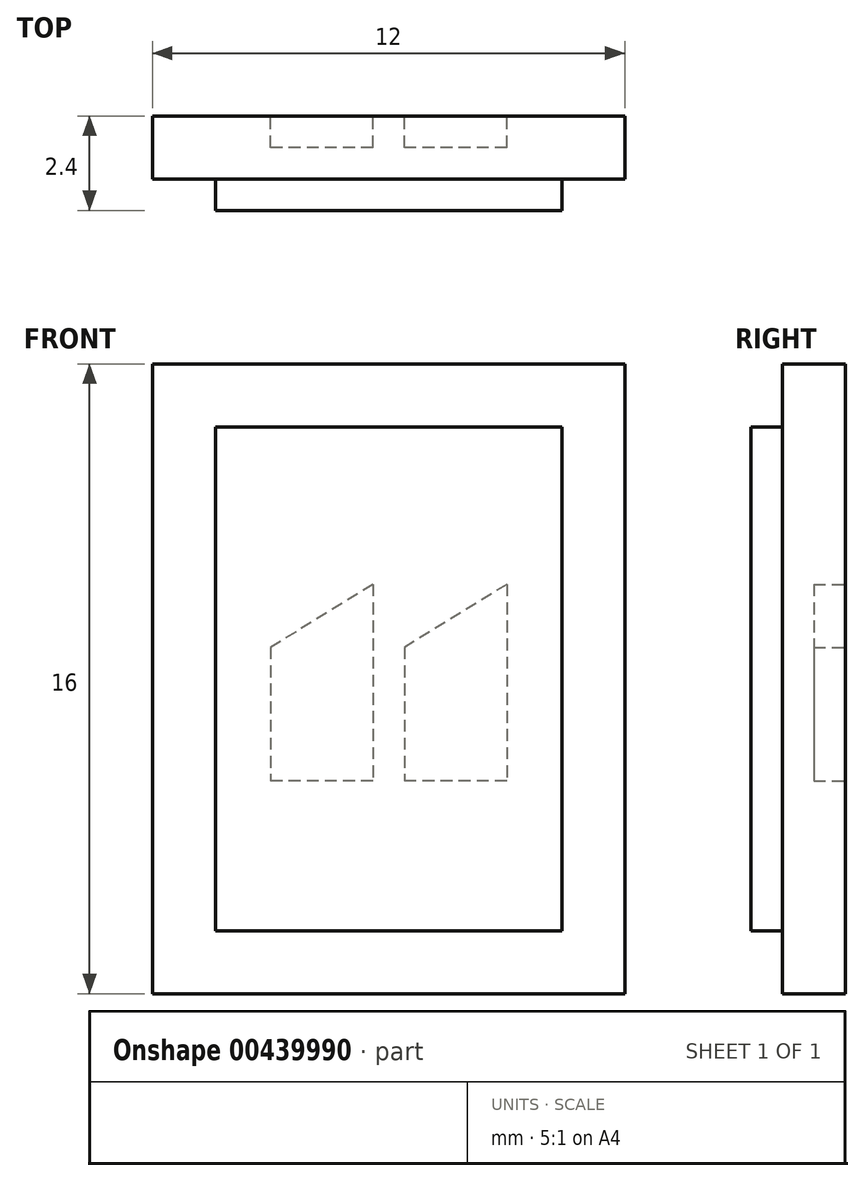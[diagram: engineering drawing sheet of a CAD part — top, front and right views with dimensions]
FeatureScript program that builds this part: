
annotation { "Feature Type Name" : "Feature", "Feature Type Description" : "" }
export const myFeature = defineFeature(function(context is Context, id is Id, definition is map)
    precondition{}
    {
        {
            var Q0;
            Q0=qCreatedBy(makeId("Front.planeOp"),FACE);
            var sketch = newSketch(context, id + "F0", { "sketchPlane" : qUnion([Q0])});
            skLineSegment(sketch, "E0.bottom", {"start": v(0, 0) * mm, "end": v(-12, 0) * mm});
            skLineSegment(sketch, "E0.top", {"start": v(0, 16) * mm, "end": v(-12, 16) * mm});
            skLineSegment(sketch, "E0.left", {"start": v(0, 0) * mm, "end": v(0, 16) * mm});
            skLineSegment(sketch, "E0.right", {"start": v(-12, 0) * mm, "end": v(-12, 16) * mm});
            skLineSegment(sketch, "E1.0", {"start": v(-1.6, 14.4) * mm, "end": v(-10.4, 14.4) * mm});
            skLineSegment(sketch, "E1.1", {"start": v(-1.6, 1.6) * mm, "end": v(-1.6, 14.4) * mm});
            skLineSegment(sketch, "E1.2", {"start": v(-1.6, 1.6) * mm, "end": v(-10.4, 1.6) * mm});
            skLineSegment(sketch, "E1.3", {"start": v(-10.4, 1.6) * mm, "end": v(-10.4, 14.4) * mm});
            skLineSegment(sketch, "E2.bottom", {"start": v(-3, 10.4) * mm, "end": v(-5.6, 10.4) * mm});
            skLineSegment(sketch, "E2.top", {"start": v(-3, 5.4) * mm, "end": v(-5.6, 5.4) * mm});
            skLineSegment(sketch, "E2.left", {"start": v(-3, 10.4) * mm, "end": v(-3, 5.4) * mm});
            skLineSegment(sketch, "E2.right", {"start": v(-5.6, 10.4) * mm, "end": v(-5.6, 5.4) * mm});
            skLineSegment(sketch, "E3.bottom", {"start": v(-6.4, 10.4) * mm, "end": v(-9, 10.4) * mm});
            skLineSegment(sketch, "E3.top", {"start": v(-6.4, 5.4) * mm, "end": v(-9, 5.4) * mm});
            skLineSegment(sketch, "E3.left", {"start": v(-6.4, 10.4) * mm, "end": v(-6.4, 5.4) * mm});
            skLineSegment(sketch, "E3.right", {"start": v(-9, 10.4) * mm, "end": v(-9, 5.4) * mm});
            skPoint(sketch, "E4", {"position": v(-5.6, 8.8) * mm});
            skPoint(sketch, "E5", {"position": v(-9, 8.8) * mm});
            skLineSegment(sketch, "E6", {"start": v(-3, 10.4) * mm, "end": v(-5.6, 8.8) * mm});
            skLineSegment(sketch, "E7", {"start": v(-6.4, 10.4) * mm, "end": v(-9, 8.8) * mm});
            skSolve(sketch);
        }
        {
            var Q0;
            Q0=makeQuery(id+"F0.imprint","IMPRINT",FACE,{"disambiguationData":[TD([[makeQuery(id+"F0.imprint","IMPRINT",EDGE,{"derivedFrom":sQuery(id+"F0.wireOp",EDGE,"E0.bottom")}),-1.0]])]});
            extrude(context, id + "F1", {"entities" : qUnion([Q0]), "depth" : 1.6 * mm});
        }
        {
            var Q0;
            Q0=makeQuery(id+"F0.imprint","IMPRINT",FACE,{"disambiguationData":[TD([[makeQuery(id+"F0.imprint","IMPRINT",EDGE,{"derivedFrom":sQuery(id+"F0.wireOp",EDGE,"E1.0")}),1.0]])]});
            var Q1;
            {var subQ0=sQuery(id+"F0.wireOp",EDGE,"E2.top");Q1=makeQuery(id+"F0.imprint","IMPRINT",FACE,{"disambiguationData":[TD([[makeQuery(id+"F0.imprint","IMPRINT",EDGE,{"derivedFrom":subQ0}),-1.0]])]});}
            var Q2;
            {var subQ0=sQuery(id+"F0.wireOp",EDGE,"E2.bottom");Q2=makeQuery(id+"F0.imprint","IMPRINT",FACE,{"disambiguationData":[TD([[makeQuery(id+"F0.imprint","IMPRINT",EDGE,{"derivedFrom":subQ0}),1.0]])]});}
            var Q3;
            {var subQ0=sQuery(id+"F0.wireOp",EDGE,"E3.top");Q3=makeQuery(id+"F0.imprint","IMPRINT",FACE,{"disambiguationData":[TD([[makeQuery(id+"F0.imprint","IMPRINT",EDGE,{"derivedFrom":subQ0}),-1.0]])]});}
            var Q4;
            {var subQ0=sQuery(id+"F0.wireOp",EDGE,"E3.bottom");Q4=makeQuery(id+"F0.imprint","IMPRINT",FACE,{"disambiguationData":[TD([[makeQuery(id+"F0.imprint","IMPRINT",EDGE,{"derivedFrom":subQ0}),1.0]])]});}
            extrude(context, id + "F2", {"entities" : qUnion([Q0, Q1, Q2, Q3, Q4]), "operationType" : NewBodyOperationType.ADD, "depth" : 2.4 * mm});
        }
        {
            var Q0;
            {var subQ0=sQuery(id+"F0.wireOp",EDGE,"E2.top");Q0=makeQuery(id+"F0.imprint","IMPRINT",FACE,{"disambiguationData":[TD([[makeQuery(id+"F0.imprint","IMPRINT",EDGE,{"derivedFrom":subQ0}),-1.0]])]});}
            var Q1;
            {var subQ0=sQuery(id+"F0.wireOp",EDGE,"E3.top");Q1=makeQuery(id+"F0.imprint","IMPRINT",FACE,{"disambiguationData":[TD([[makeQuery(id+"F0.imprint","IMPRINT",EDGE,{"derivedFrom":subQ0}),-1.0]])]});}
            extrude(context, id + "F3", {"entities" : qUnion([Q0, Q1]), "operationType" : NewBodyOperationType.REMOVE, "depth" : 0.8 * mm});
        }
    });
